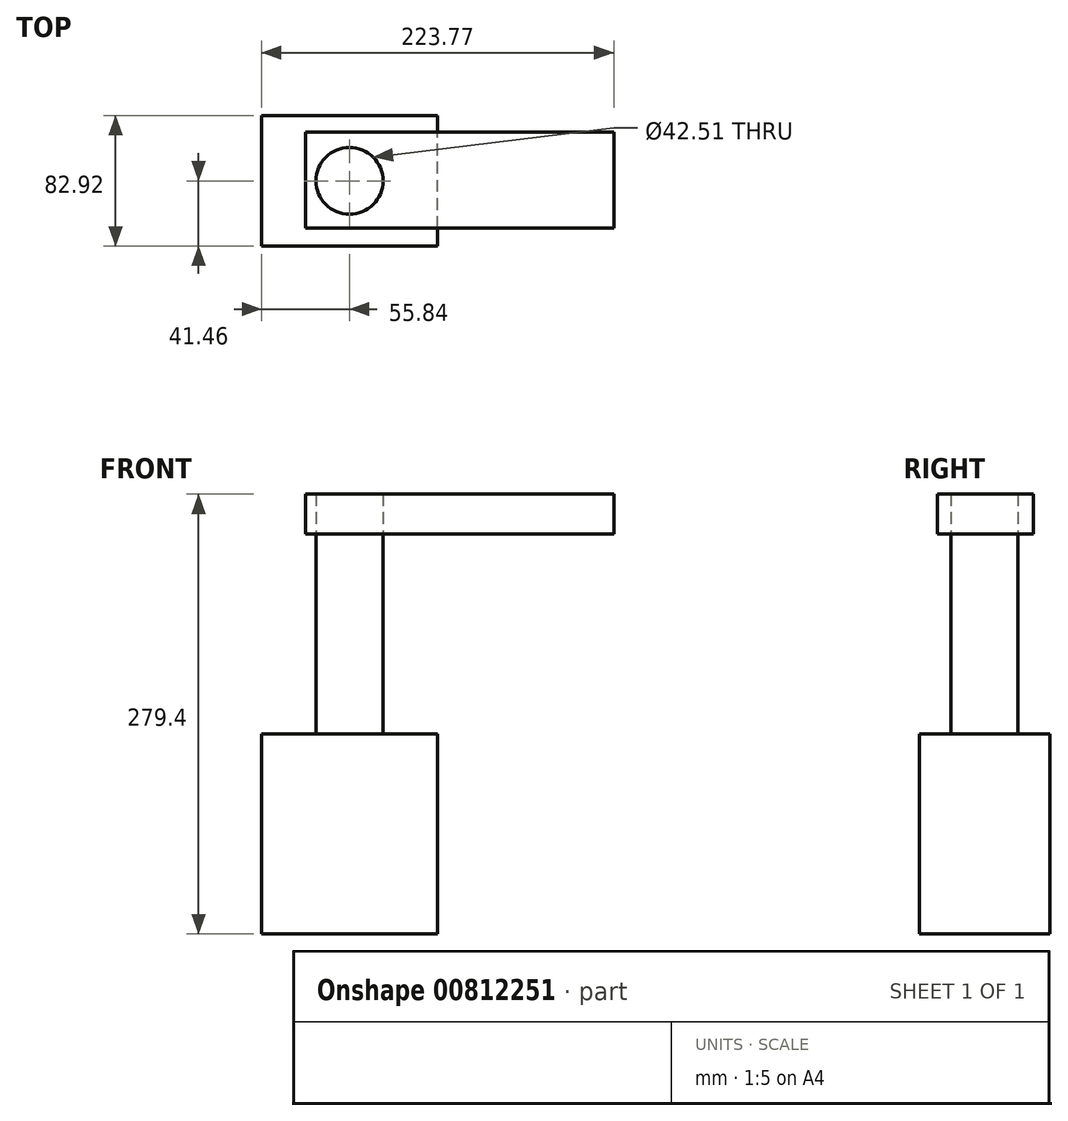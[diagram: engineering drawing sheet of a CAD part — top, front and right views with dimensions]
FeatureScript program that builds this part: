
annotation { "Feature Type Name" : "Feature", "Feature Type Description" : "" }
export const myFeature = defineFeature(function(context is Context, id is Id, definition is map)
    precondition{}
    {
        {
            var Q0;
            Q0=qCreatedBy(makeId("Top.planeOp"),FACE);
            var sketch = newSketch(context, id + "F0", { "sketchPlane" : qUnion([Q0])});
            skLineSegment(sketch, "E0.bottom", {"start": v(55.84, -41.46) * mm, "end": v(-55.84, -41.46) * mm});
            skLineSegment(sketch, "E0.top", {"start": v(55.84, 41.46) * mm, "end": v(-55.84, 41.46) * mm});
            skLineSegment(sketch, "E0.left", {"start": v(55.84, -41.46) * mm, "end": v(55.84, 41.46) * mm});
            skLineSegment(sketch, "E0.right", {"start": v(-55.84, -41.46) * mm, "end": v(-55.84, 41.46) * mm});
            skPoint(sketch, "E0.middle", {"position": v(0, 0) * mm});
            skSolve(sketch);
        }
        {
            var Q0;
            Q0 = qSketchRegion(id + "F0", true);
            extrude(context, id + "F1", {"entities" : qUnion([Q0]), "depth" : 127 * mm, "offsetDistance" : 25.4 * mm});
        }
        {
            var Q0;
            Q0=makeQuery(id+"F1.opExtrude","CAP_FACE",FACE,{"disambiguationData":[OSD([sQuery(id+"F0.wireOp",EDGE,"E0.bottom"),sQuery(id+"F0.wireOp",EDGE,"E0.top"),sQuery(id+"F0.wireOp",EDGE,"E0.left"),sQuery(id+"F0.wireOp",EDGE,"E0.right")])],"isStart":false});
            var sketch = newSketch(context, id + "F2", { "sketchPlane" : qUnion([Q0])});
            skCircle(sketch, "E1", {"center": v(0, 0) * mm, "radius": 21.26 * mm});
            skSolve(sketch);
        }
        {
            var Q0;
            Q0=makeQuery(id+"F2.imprint","IMPRINT",FACE,{"disambiguationData":[TD([[makeQuery(id+"F2.imprint","IMPRINT",EDGE,{"derivedFrom":sQuery(id+"F2.wireOp",EDGE,"E1")}),1.0]])]});
            extrude(context, id + "F3", {"entities" : qUnion([Q0]), "depth" : 127 * mm, "offsetDistance" : 25.4 * mm});
        }
        {
            var Q0;
            Q0=makeQuery(id+"F3.opExtrude","CAP_FACE",FACE,{"disambiguationData":[OSD([sQuery(id+"F2.wireOp",EDGE,"E1")])],"isStart":false});
            var sketch = newSketch(context, id + "F4", { "sketchPlane" : qUnion([Q0])});
            skLineSegment(sketch, "E2.bottom", {"start": v(-27.84, 31.07) * mm, "end": v(167.93, 31.07) * mm});
            skLineSegment(sketch, "E2.top", {"start": v(-27.84, -29.9) * mm, "end": v(167.93, -29.9) * mm});
            skLineSegment(sketch, "E2.left", {"start": v(-27.84, 31.07) * mm, "end": v(-27.84, -29.9) * mm});
            skLineSegment(sketch, "E2.right", {"start": v(167.93, 31.07) * mm, "end": v(167.93, -29.9) * mm});
            skSolve(sketch);
        }
        {
            var Q0;
            Q0=makeQuery(id+"F4.imprint","IMPRINT",FACE,{"disambiguationData":[TD([[makeQuery(id+"F4.imprint","IMPRINT",EDGE,{"derivedFrom":sQuery(id+"F4.wireOp",EDGE,"E2.bottom")}),-1.0]])]});
            extrude(context, id + "F5", {"entities" : qUnion([Q0]), "depth" : 25.4 * mm, "offsetDistance" : 25.4 * mm});
        }
    });
